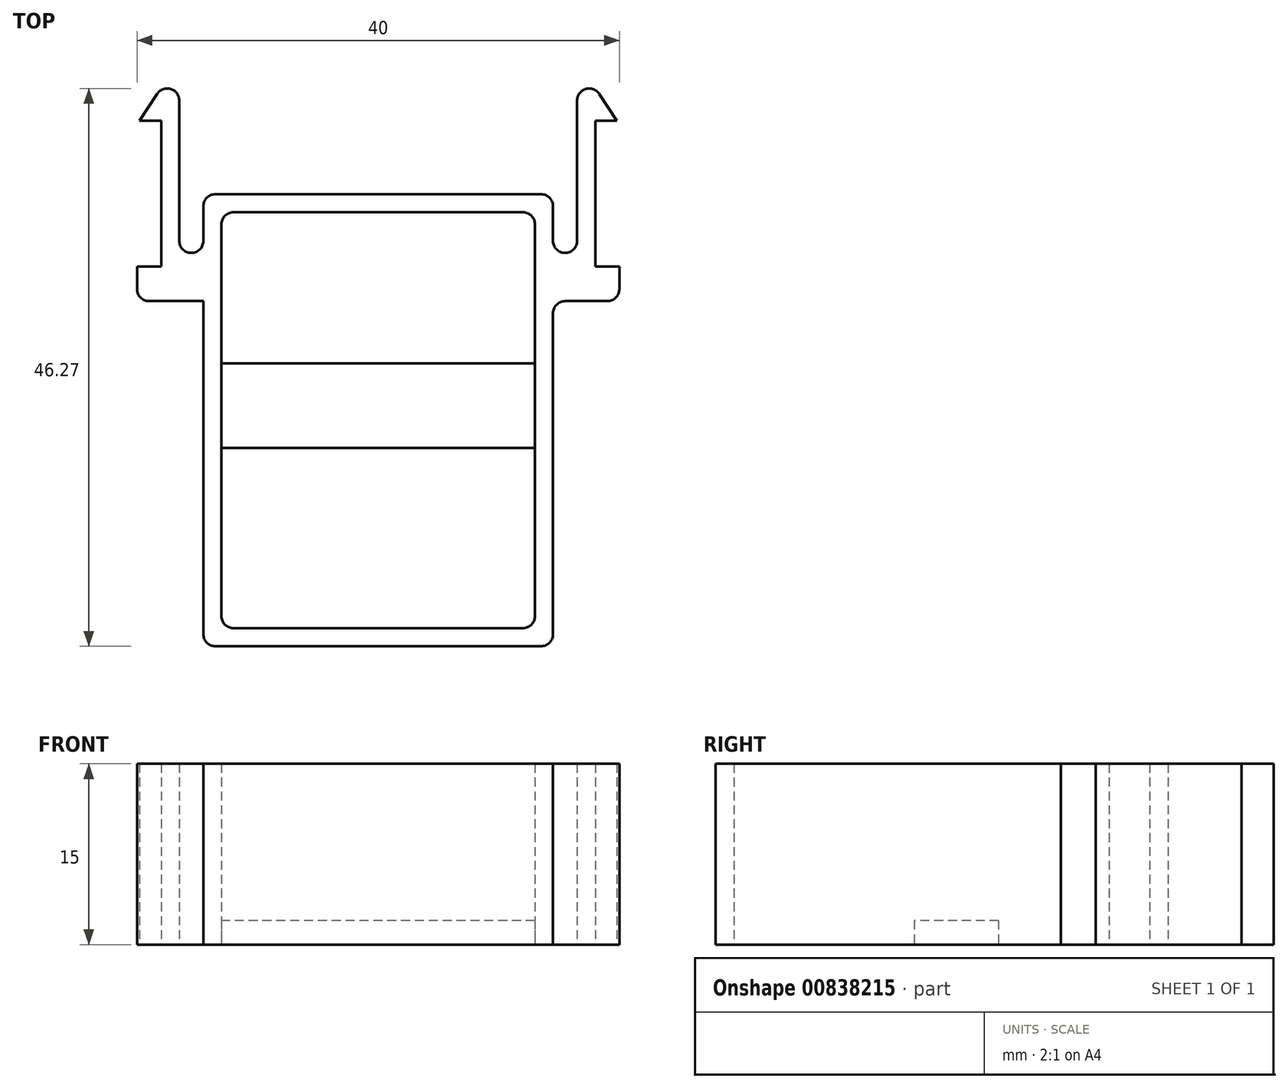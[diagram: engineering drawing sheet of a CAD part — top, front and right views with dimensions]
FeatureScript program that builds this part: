
annotation { "Feature Type Name" : "Feature", "Feature Type Description" : "" }
export const myFeature = defineFeature(function(context is Context, id is Id, definition is map)
    precondition{}
    {
        {
            var Q0;
            Q0=qCreatedBy(makeId("Top.planeOp"),FACE);
            var sketch = newSketch(context, id + "F0", { "sketchPlane" : qUnion([Q0])});
            skLineSegment(sketch, "E0.bottom", {"start": v(-13, 17.25) * mm, "end": v(13, 17.25) * mm});
            skLineSegment(sketch, "E0.top", {"start": v(-13, -17.25) * mm, "end": v(13, -17.25) * mm});
            skLineSegment(sketch, "E0.left", {"start": v(-13, 17.25) * mm, "end": v(-13, -17.25) * mm});
            skLineSegment(sketch, "E0.right", {"start": v(13, 17.25) * mm, "end": v(13, -17.25) * mm});
            skPoint(sketch, "E0.middle", {"position": v(0, 0) * mm});
            skLineSegment(sketch, "E1.0", {"start": v(-14.5, 18.75) * mm, "end": v(-14.5, -18.75) * mm});
            skLineSegment(sketch, "E1.1", {"start": v(-14.5, 18.75) * mm, "end": v(14.5, 18.75) * mm});
            skLineSegment(sketch, "E1.2", {"start": v(14.5, 18.75) * mm, "end": v(14.5, -18.75) * mm});
            skLineSegment(sketch, "E1.3", {"start": v(-14.5, -18.75) * mm, "end": v(14.5, -18.75) * mm});
            skLineSegment(sketch, "E2", {"start": v(0, -36.25) * mm, "end": v(0, 59.39) * mm, "construction": true});
            skLineSegment(sketch, "E3", {"start": v(-14.5, 9.88) * mm, "end": v(-16.5, 9.88) * mm});
            skLineSegment(sketch, "E4", {"start": v(-16.5, 9.88) * mm, "end": v(-16.5, 13.88) * mm});
            skLineSegment(sketch, "E5", {"start": v(-16.5, 13.88) * mm, "end": v(-14.5, 13.88) * mm});
            skLineSegment(sketch, "E6", {"start": v(-16.5, 9.88) * mm, "end": v(-16.5, 29.86) * mm});
            skLineSegment(sketch, "E7", {"start": v(-16.5, 29.86) * mm, "end": v(-19.8, 24.85) * mm});
            skLineSegment(sketch, "E8", {"start": v(-19.8, 24.85) * mm, "end": v(-18, 24.85) * mm});
            skLineSegment(sketch, "E9", {"start": v(-18, 24.85) * mm, "end": v(-18, 9.88) * mm});
            skLineSegment(sketch, "E10", {"start": v(-18, 9.88) * mm, "end": v(-16.5, 9.88) * mm});
            skLineSegment(sketch, "E11", {"start": v(-18, 9.88) * mm, "end": v(-20, 9.88) * mm});
            skLineSegment(sketch, "E12", {"start": v(-20, 9.88) * mm, "end": v(-20, 12.75) * mm});
            skLineSegment(sketch, "E13", {"start": v(-20, 12.75) * mm, "end": v(-18, 12.75) * mm});
            skLineSegment(sketch, "E14.MirrorCS", {"start": v(16.5, 9.88) * mm, "end": v(16.5, 29.86) * mm});
            skLineSegment(sketch, "E15.MirrorCS", {"start": v(16.5, 29.86) * mm, "end": v(19.8, 24.85) * mm});
            skLineSegment(sketch, "E16.MirrorCS", {"start": v(18, 24.85) * mm, "end": v(18, 9.88) * mm});
            skLineSegment(sketch, "E17.MirrorCS", {"start": v(20, 12.75) * mm, "end": v(18, 12.75) * mm});
            skLineSegment(sketch, "E18.MirrorCS", {"start": v(20, 9.88) * mm, "end": v(20, 12.75) * mm});
            skLineSegment(sketch, "E19.MirrorCS", {"start": v(18, 9.88) * mm, "end": v(20, 9.88) * mm});
            skLineSegment(sketch, "E20.MirrorCS", {"start": v(18, 9.88) * mm, "end": v(16.5, 9.88) * mm});
            skLineSegment(sketch, "E21.MirrorCS", {"start": v(14.5, 9.88) * mm, "end": v(16.5, 9.88) * mm});
            skLineSegment(sketch, "E22.MirrorCS", {"start": v(16.5, 13.88) * mm, "end": v(14.5, 13.88) * mm});
            skLineSegment(sketch, "E23.MirrorCS", {"start": v(19.8, 24.85) * mm, "end": v(18, 24.85) * mm});
            skLineSegment(sketch, "E24", {"start": v(-13, -2.29) * mm, "end": v(13, -2.29) * mm});
            skLineSegment(sketch, "E25", {"start": v(13, -2.29) * mm, "end": v(13, 4.71) * mm});
            skLineSegment(sketch, "E26", {"start": v(13, 4.71) * mm, "end": v(-13, 4.71) * mm});
            skSolve(sketch);
        }
        {
            var Q0;
            Q0 = qSketchRegion(id + "F0", true);
            extrude(context, id + "F1", {"entities" : qUnion([Q0]), "depth" : 15 * mm, "offsetDistance" : 25 * mm});
        }
        {
            var Q0;
            Q0=makeQuery(id+"F1.opExtrude","SWEPT_EDGE",EDGE,{"disambiguationData":[OSD([sQuery(id+"F0.wireOp",EDGE,"E1.0"),sQuery(id+"F0.wireOp",EDGE,"E1.1")])]});
            var Q1;
            Q1=makeQuery(id+"F1.opExtrude","SWEPT_EDGE",EDGE,{"disambiguationData":[OSD([sQuery(id+"F0.wireOp",EDGE,"E11"),sQuery(id+"F0.wireOp",EDGE,"E12")])]});
            var Q2;
            Q2=makeQuery(id+"F1.opExtrude","SWEPT_EDGE",EDGE,{"disambiguationData":[OSD([sQuery(id+"F0.wireOp",EDGE,"E1.1"),sQuery(id+"F0.wireOp",EDGE,"E1.2")])]});
            var Q3;
            Q3=makeQuery(id+"F1.opExtrude","SWEPT_EDGE",EDGE,{"disambiguationData":[OSD([sQuery(id+"F0.wireOp",EDGE,"E18.MirrorCS"),sQuery(id+"F0.wireOp",EDGE,"E19.MirrorCS")])]});
            var Q4;
            Q4=makeQuery(id+"F1.opExtrude","SWEPT_EDGE",EDGE,{"disambiguationData":[OSD([sQuery(id+"F0.wireOp",EDGE,"E0.bottom"),sQuery(id+"F0.wireOp",EDGE,"E0.left")])]});
            var Q5;
            Q5=makeQuery(id+"F1.opExtrude","SWEPT_EDGE",EDGE,{"disambiguationData":[OSD([sQuery(id+"F0.wireOp",EDGE,"E1.2"),sQuery(id+"F0.wireOp",EDGE,"E21.MirrorCS")])]});
            var Q6;
            Q6=makeQuery(id+"F1.opExtrude","SWEPT_EDGE",EDGE,{"disambiguationData":[OSD([sQuery(id+"F0.wireOp",EDGE,"E1.2"),sQuery(id+"F0.wireOp",EDGE,"E1.3")])]});
            var Q7;
            Q7=makeQuery(id+"F1.opExtrude","SWEPT_EDGE",EDGE,{"disambiguationData":[OSD([sQuery(id+"F0.wireOp",EDGE,"E1.0"),sQuery(id+"F0.wireOp",EDGE,"E1.3")])]});
            var Q8;
            Q8=makeQuery(id+"F1.opExtrude","SWEPT_EDGE",EDGE,{"disambiguationData":[OSD([sQuery(id+"F0.wireOp",EDGE,"E0.top"),sQuery(id+"F0.wireOp",EDGE,"E0.left")])]});
            var Q9;
            Q9=makeQuery(id+"F1.opExtrude","SWEPT_EDGE",EDGE,{"disambiguationData":[OSD([sQuery(id+"F0.wireOp",EDGE,"E0.bottom"),sQuery(id+"F0.wireOp",EDGE,"E0.right")])]});
            var Q10;
            Q10=makeQuery(id+"F1.opExtrude","SWEPT_EDGE",EDGE,{"disambiguationData":[OSD([sQuery(id+"F0.wireOp",EDGE,"E0.top"),sQuery(id+"F0.wireOp",EDGE,"E0.right")])]});
            var Q11;
            Q11=makeQuery(id+"F1.opExtrude","SWEPT_EDGE",EDGE,{"disambiguationData":[OSD([sQuery(id+"F0.wireOp",EDGE,"E1.0"),sQuery(id+"F0.wireOp",EDGE,"E5")])]});
            var Q12;
            Q12=makeQuery(id+"F1.opExtrude","SWEPT_EDGE",EDGE,{"disambiguationData":[OSD([sQuery(id+"F0.wireOp",EDGE,"E14.MirrorCS"),sQuery(id+"F0.wireOp",EDGE,"E22.MirrorCS")])]});
            var Q13;
            Q13=makeQuery(id+"F1.opExtrude","SWEPT_EDGE",EDGE,{"disambiguationData":[OSD([sQuery(id+"F0.wireOp",EDGE,"E5"),sQuery(id+"F0.wireOp",EDGE,"E6")])]});
            var Q14;
            Q14=makeQuery(id+"F1.opExtrude","SWEPT_EDGE",EDGE,{"disambiguationData":[OSD([sQuery(id+"F0.wireOp",EDGE,"E1.2"),sQuery(id+"F0.wireOp",EDGE,"E22.MirrorCS")])]});
            var Q15;
            Q15=makeQuery(id+"F1.opExtrude","SWEPT_EDGE",EDGE,{"disambiguationData":[OSD([sQuery(id+"F0.wireOp",EDGE,"E6"),sQuery(id+"F0.wireOp",EDGE,"E7")])]});
            var Q16;
            Q16=makeQuery(id+"F1.opExtrude","SWEPT_EDGE",EDGE,{"disambiguationData":[OSD([sQuery(id+"F0.wireOp",EDGE,"E14.MirrorCS"),sQuery(id+"F0.wireOp",EDGE,"E15.MirrorCS")])]});
            fillet(context, id + "F2", {"entities" : qUnion([Q0, Q1, Q2, Q3, Q4, Q5, Q6, Q7, Q8, Q9, Q10, Q11, Q12, Q13, Q14, Q15, Q16]), "radius" : 1 * mm, "tangentPropagation" : true, "allowEdgeOverflow" : false});
        }
        {
            var Q0;
            {var subQ0=sQuery(id+"F0.wireOp",EDGE,"E24");Q0=makeQuery(id+"F0.imprint","IMPRINT",FACE,{"disambiguationData":[TD([[makeQuery(id+"F0.imprint","IMPRINT",EDGE,{"derivedFrom":subQ0}),1.0]])]});}
            extrude(context, id + "F3", {"entities" : qUnion([Q0]), "operationType" : NewBodyOperationType.ADD, "depth" : 2 * mm, "offsetDistance" : 25 * mm});
        }
    });
